# Revit family: Lighting-Industriale-GEWISS-ESALITE-HB-APPARECCHI-LED_6K_EMERGENZA
name_source: partatom
category: Apparecchi per illuminazione
units: mm (PartAtom-declared; Revit-internal decimal feet)

## family parameters
Condiviso = No
Host = Superficie
Punto di calcolo locali = Sì
Quota connettore circolare = Usa diametro
Sorgente d'illuminazione = No
Taglio con vuoti quando caricato = No
Tipo di parte = Normale

## types (1)
- Lighting-Industriale-GEWISS-ESALITE-HB-APPARECCHI-LED_6K_EMERGENZA
    Apparecchio a ridotta temperatura superficiale = Conforme
    Applicazione = Interno
    Autonomia: = 3H
    Catalogo = LIGHTING
    Catalogo Serie = ESALITE HB - 6K
    Certificazione DIN 18032-3 = No
    Classe di efficienza LED integrati = A ÷ A++
    Classe isolamento = I
    Codice Electrocod = 2444
    Colore = Grigio RAL 9006 + 7035
    Corrente di pilotaggio LED = 0,6A
    Corrente di pilotaggio. = 0,599999999999999A
    Descrizione = ESALITE HB 6K 90° 4000K EMERG.3H CRI80
    Descrizione: = Esalite HB 6k con lente ed Emergenza 3h – 4000K (CRI80)
    Flusso luminoso in emergenza (lm) = 650
    Flusso nominale (lm) = 7200
    Garanzia = 5 anni
    Glow Wire Test = 650°C
    Grado di protezione = IP55
    IDF = ba228690-660b-45e8-9cec-37ef7f12a3f1
    IDT = e1623446787a4785a8c69eeae9ffe9d2
    Immagine tipo = ESALITE_HB.jpg
    Lampada: = LED - Non sostituibile
    Life time L90B10 (Tq 25°C) = 100000H
    Life time L90B10 (Tq 50°C) = 55000H
    Lumen output (lm) = 6700
    Lumen output in ordinaria (lm) = 6700
    Modello = GWS6911
    Numero poli = 1
    Ottica = 90°
    Peso (kg): = 4,5
    Potenza di sistema = 60W
    Potenza di sitema = Wxxx
    Produttore = GEWISS S.p.A.
    Prospetto di default = 1219 mm
    Resistenza agli urti = IK06
    SEO = High bay
    Scheda Tecnica = https://www.gewiss.com
    Schermo = Plastico
    Temperatura di colore: = 4000 K (CRI>80)
    Temperatura di utilizzo = 0 ÷ +40 °C
    Tensione = 220/240 V - 50/60 Hz
    Tipo alimentatore = Driver Dali
    Tipo versione = Emergenza
    Tipologia = Emergenza
    Tipologia sorgente luminosa = LED - Non sostituibile
    URL = https://www.gewiss.com
    V = 0 V
    Versione file RFA = 20.11
    Versioni = Luce naturale 4000K
